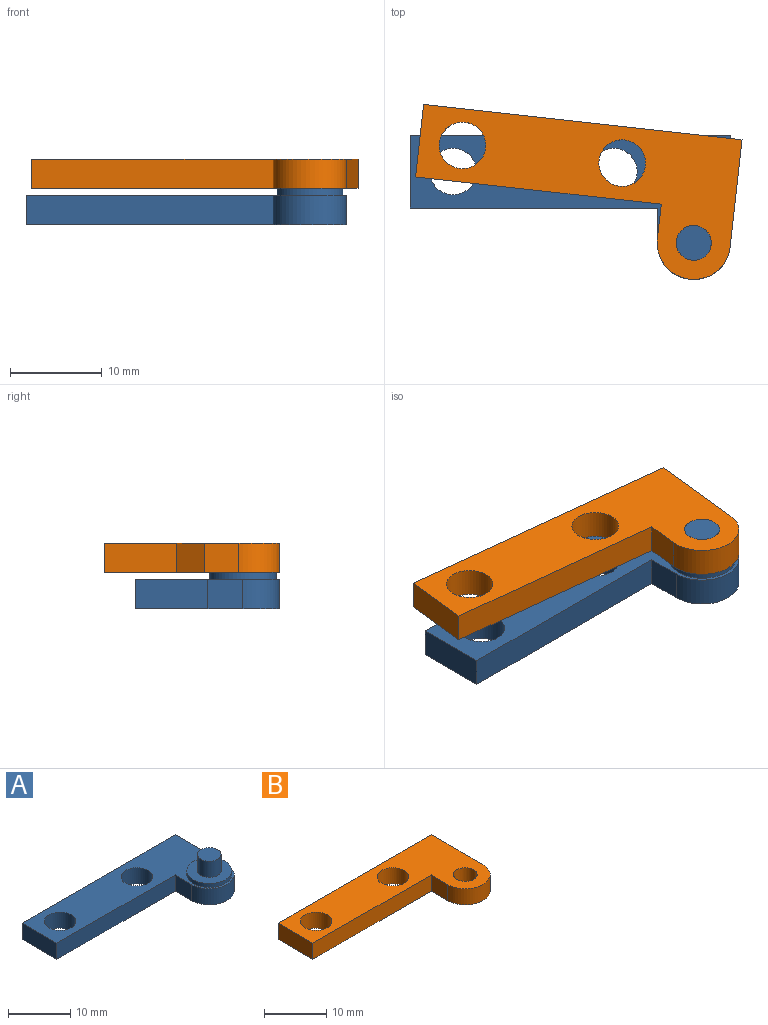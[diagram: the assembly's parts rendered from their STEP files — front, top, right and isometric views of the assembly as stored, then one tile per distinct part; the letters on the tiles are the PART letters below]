
ASSEMBLY  parts=2 mates=2
PART A: 14 faces, bbox 34.9x15.7x7.1 mm
  f0: cylinder r=3.99mm len=7.98mm, axis (0,0,-1), area 39.8mm2, adj f1,f6,f8,f9
  f1: plane 11.76x3.18mm, normal (1,0,0), area 37.3mm2, adj f0,f2,f8,f9
  f2: plane 34.93x3.18mm, normal (0,1,0), area 110.9mm2, adj f1,f3,f8,f9
  f3: plane 7.95x3.18mm, normal (-1,0,0), area 25.2mm2, adj f2,f4,f8,f9
  f4: plane 26.95x3.18mm, normal (0,-1,0), area 85.6mm2, adj f3,f6,f8,f9
  f5: cylinder r=2.54mm len=5.08mm, axis (0,0,-1), area 50.7mm2, adj f8,f9
  f6: plane 3.81x3.18mm, normal (-1,0,0), area 12.1mm2, adj f0,f4,f8,f9
  f7: cylinder r=2.54mm len=5.08mm, axis (0,0,-1), area 50.7mm2, adj f8,f9
  f8: plane 34.93x15.75mm, normal (0,0,1), area 251.3mm2, adj f0,f1,f2,f3,f4,f5,f6,f7
  f9: plane 34.93x15.75mm, normal (0,0,-1), area 292.5mm2, adj f0,f1,f2,f3,f4,f5,f6,f7
  f10: cylinder r=3.62mm len=7.24mm, axis (0,0,-1), area 17.9mm2, adj f8,f11
  f11: plane 7.24x7.24mm, normal (0,0,1), area 29.8mm2, adj f10,f12
  f12: cylinder r=1.91mm len=3.81mm, axis (0,0,-1), area 38mm2, adj f11,f13
  f13: plane 3.81x3.81mm, normal (0,0,1), area 11.4mm2, adj f12
PART B: 11 faces, bbox 34.9x15.7x3.2 mm
  f0: cylinder r=3.99mm len=7.98mm, axis (0,0,-1), area 39.8mm2, adj f1,f7,f9,f10
  f1: plane 11.76x3.18mm, normal (1,0,0), area 37.3mm2, adj f0,f2,f9,f10
  f2: plane 34.93x3.18mm, normal (0,1,0), area 110.9mm2, adj f1,f3,f9,f10
  f3: plane 7.95x3.18mm, normal (-1,0,0), area 25.2mm2, adj f2,f4,f9,f10
  f4: plane 26.95x3.18mm, normal (0,-1,0), area 85.6mm2, adj f3,f7,f9,f10
  f5: cylinder r=2.54mm len=5.08mm, axis (0,0,-1), area 50.7mm2, adj f9,f10
  f6: cylinder r=2.54mm len=5.08mm, axis (0,0,-1), area 50.7mm2, adj f9,f10
  f7: plane 3.81x3.18mm, normal (-1,0,0), area 12.1mm2, adj f0,f4,f9,f10
  f8: cylinder r=1.91mm len=3.81mm, axis (0,0,-1), area 38mm2, adj f9,f10
  f9: plane 34.93x15.75mm, normal (0,0,1), area 281.1mm2, adj f0,f1,f2,f3,f4,f5,f6,f7
  f10: plane 34.93x15.75mm, normal (0,0,-1), area 281.1mm2, adj f0,f1,f2,f3,f4,f5,f6,f7
PLACE A at identity fixed
PLACE B rot(axis=(0,0,-1),6.3deg) t=(0,0,3.96)mm
MATE cylindrical B.f8 <-> A.f12  axis (0,0,-1) through (0,0,7.14)mm
MATE planar B.f10 <-> A.f10  axis (0,0,-1) through (-10,7.77,3.96)mm
